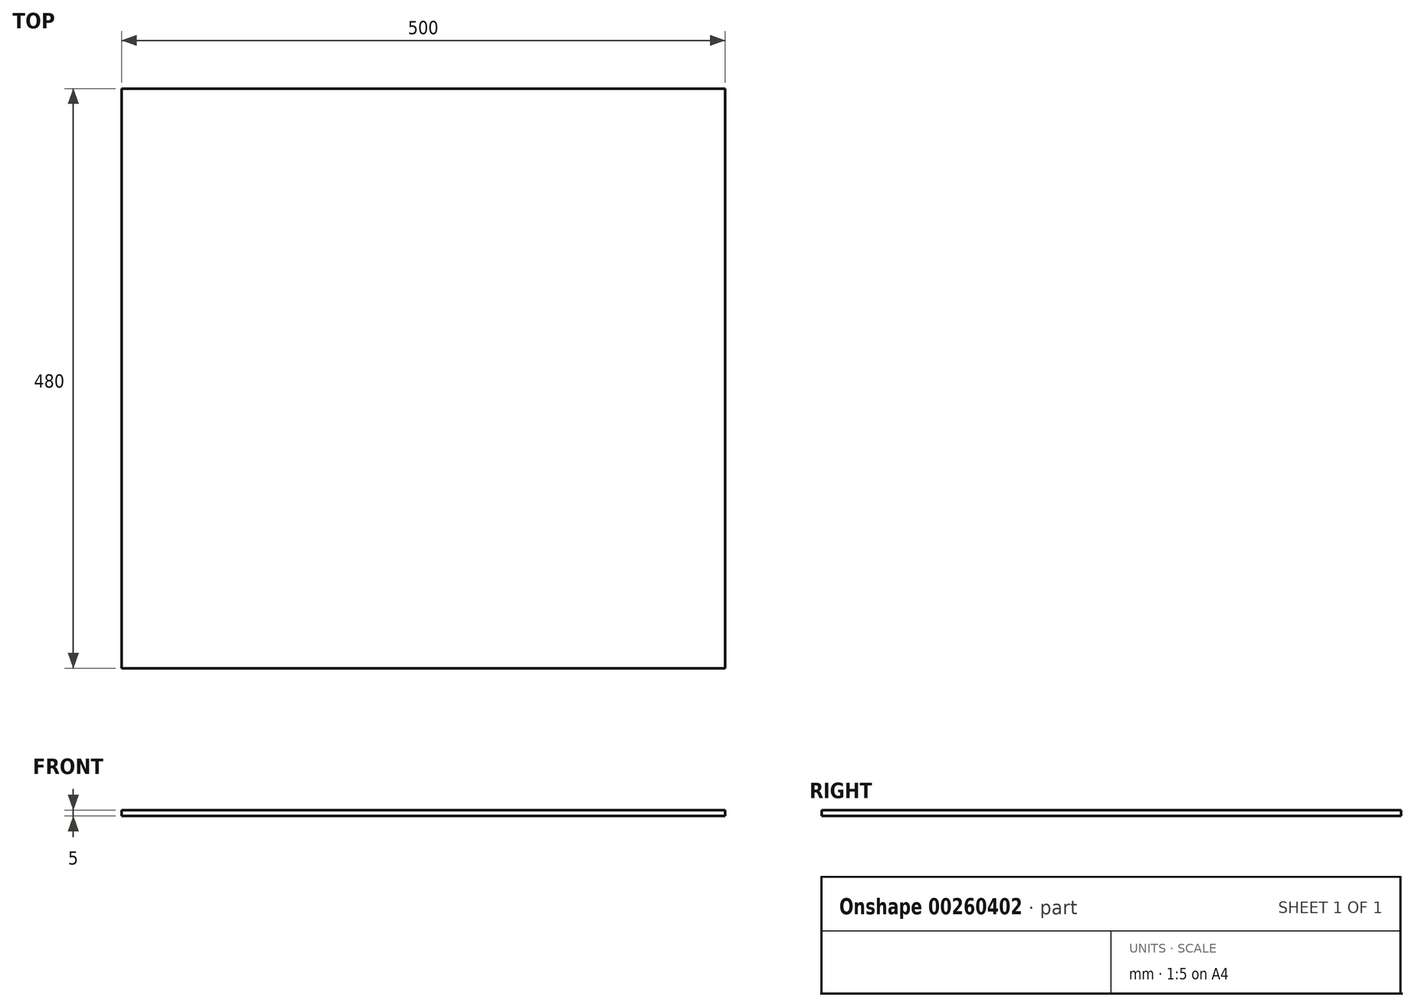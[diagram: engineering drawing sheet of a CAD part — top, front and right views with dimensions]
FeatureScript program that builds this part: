
annotation { "Feature Type Name" : "Feature", "Feature Type Description" : "" }
export const myFeature = defineFeature(function(context is Context, id is Id, definition is map)
    precondition{}
    {
        {
            var Q0;
            Q0=qCreatedBy(makeId("Top.planeOp"),FACE);
            var sketch = newSketch(context, id + "F0", { "sketchPlane" : qUnion([Q0])});
            skLineSegment(sketch, "E0.bottom", {"start": v(-237.13, 250.22) * mm, "end": v(262.87, 250.22) * mm});
            skLineSegment(sketch, "E0.top", {"start": v(-237.13, -229.78) * mm, "end": v(262.87, -229.78) * mm});
            skLineSegment(sketch, "E0.left", {"start": v(-237.13, 250.22) * mm, "end": v(-237.13, -229.78) * mm});
            skLineSegment(sketch, "E0.right", {"start": v(262.87, 250.22) * mm, "end": v(262.87, -229.78) * mm});
            skSolve(sketch);
        }
        {
            var Q0;
            Q0 = qSketchRegion(id + "F0", true);
            extrude(context, id + "F1", {"entities" : qUnion([Q0]), "depth" : 5 * mm});
        }
    });
